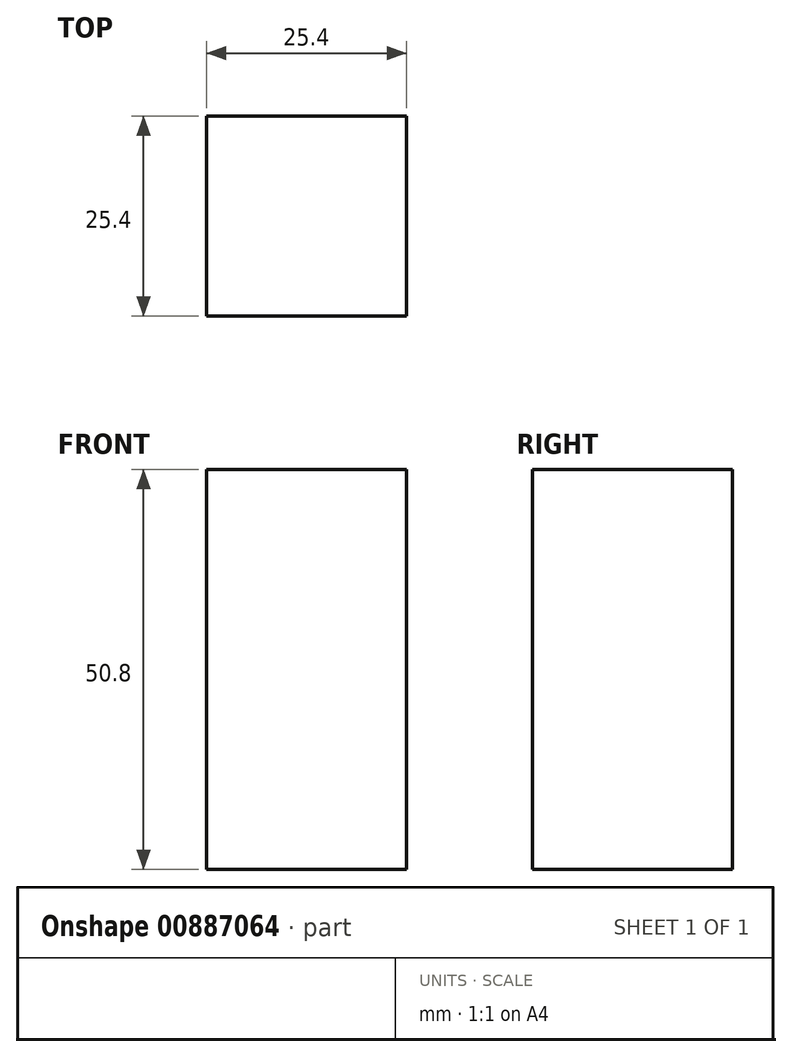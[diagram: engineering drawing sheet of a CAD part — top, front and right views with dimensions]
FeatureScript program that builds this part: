
annotation { "Feature Type Name" : "Feature", "Feature Type Description" : "" }
export const myFeature = defineFeature(function(context is Context, id is Id, definition is map)
    precondition{}
    {
        {
            var Q0;
            Q0=qCreatedBy(makeId("Front.planeOp"),FACE);
            var sketch = newSketch(context, id + "F0", { "sketchPlane" : qUnion([Q0])});
            skLineSegment(sketch, "E0.bottom", {"start": v(12.7, -25.4) * mm, "end": v(-12.7, -25.4) * mm});
            skLineSegment(sketch, "E0.top", {"start": v(12.7, 25.4) * mm, "end": v(-12.7, 25.4) * mm});
            skLineSegment(sketch, "E0.left", {"start": v(12.7, -25.4) * mm, "end": v(12.7, 25.4) * mm});
            skLineSegment(sketch, "E0.right", {"start": v(-12.7, -25.4) * mm, "end": v(-12.7, 25.4) * mm});
            skPoint(sketch, "E0.middle", {"position": v(0, 0) * mm});
            skSolve(sketch);
        }
        {
            var Q0;
            Q0 = qSketchRegion(id + "F0", true);
            extrude(context, id + "F1", {"entities" : qUnion([Q0]), "depth" : 25.4 * mm, "offsetDistance" : 25.4 * mm});
        }
    });
